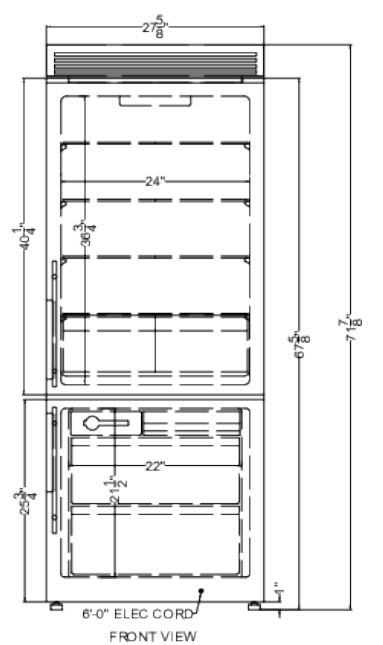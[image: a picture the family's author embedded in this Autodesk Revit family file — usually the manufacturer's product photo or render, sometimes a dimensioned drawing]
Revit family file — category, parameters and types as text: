
# Revit family: QF_Summit_FFBF279SSXH72_Freezer_Refrigerator
name_source: partatom
category: Specialty Equipment
units: mm (PartAtom-declared; Revit-internal decimal feet)

## family parameters
Always vertical = Yes
Cut with Voids When Loaded = No
Part Type = Normal
Room Calculation Point = No
Round Connector Dimension = Use Diameter
Shared = No
Work Plane-Based = No

## types (1)
- QF_Summit_FFBF279SSXH72_Freezer_Refrigerator
    Apparent Power = 0 VA
    Conn Conduit = Yes
    Cycle = 60 Hz
    Default Elevation = 0"
    Depth = 26 3/4"
    Description = Freezer Refrigerator
    Elec Conn Connection Height = 0"
    Elec Conn RI Height = 0"
    FL Amps = 2 A
    Foodservice Equipment Identifier = Yes
    Height = 71 7/8"
    Identify Quantity as Lot = Yes
    Length = 27 5/8"
    Manufacturer = Summit
    Max Overcurrent Protection = 0 A
    Min Ckt Ampacity = 0 A
    Model = FFBF279SSXH72
    Number of Poles = 1
    Phase = 1
    Volts = 115 V
    Watts = 230 W
    Weight in Pounds = 177

## geometry (parser evidence)
native form markers: Sweep x5
no freeform markers — native parametric forms only
